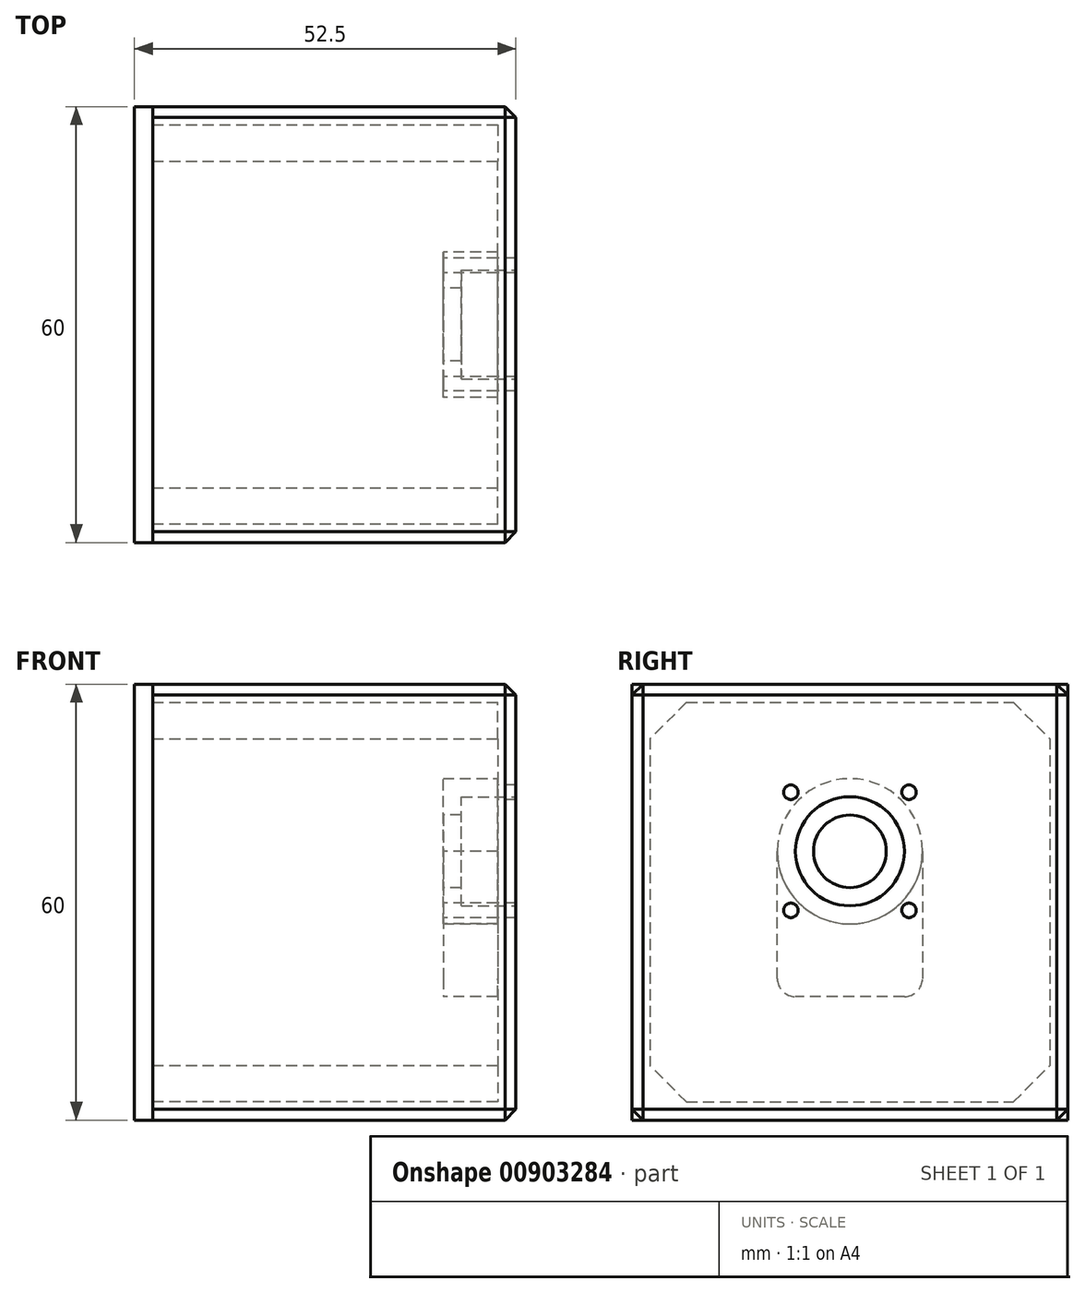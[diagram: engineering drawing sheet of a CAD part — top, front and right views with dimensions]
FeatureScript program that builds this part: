
annotation { "Feature Type Name" : "Feature", "Feature Type Description" : "" }
export const myFeature = defineFeature(function(context is Context, id is Id, definition is map)
    precondition{}
    {
        {
            var Q0;
            Q0=qCreatedBy(makeId("Right.planeOp"),FACE);
            var sketch = newSketch(context, id + "F0", { "sketchPlane" : qUnion([Q0])});
            skLineSegment(sketch, "E0.bottom", {"start": v(-30, 63) * mm, "end": v(30, 63) * mm});
            skLineSegment(sketch, "E0.top", {"start": v(-30, 3) * mm, "end": v(0, 3) * mm});
            skLineSegment(sketch, "E0.left", {"start": v(-30, 63) * mm, "end": v(-30, 3) * mm});
            skLineSegment(sketch, "E0.right", {"start": v(30, 63) * mm, "end": v(30, 3) * mm});
            skLineSegment(sketch, "E1", {"start": v(0, 0) * mm, "end": v(0, 0) * mm});
            skLineSegment(sketch, "E2", {"start": v(0, 0) * mm, "end": v(0, 3) * mm, "construction": true});
            skLineSegment(sketch, "E3", {"start": v(0, 3) * mm, "end": v(30, 3) * mm});
            skSolve(sketch);
        }
        {
            var Q0;
            Q0=makeQuery(id+"F0.imprint","IMPRINT",FACE,{"disambiguationData":[TD([[makeQuery(id+"F0.imprint","IMPRINT",EDGE,{"derivedFrom":sQuery(id+"F0.wireOp",EDGE,"E0.bottom")}),-1.0]])]});
            extrude(context, id + "F1", {"entities" : qUnion([Q0]), "depth" : 50 * mm, "offsetDistance" : 25 * mm});
        }
        {
            var Q0;
            Q0=makeQuery(id+"F1.opExtrude","CAP_FACE",FACE,{"disambiguationData":[OSD([sQuery(id+"F0.wireOp",EDGE,"E0.bottom"),sQuery(id+"F0.wireOp",EDGE,"E0.top"),sQuery(id+"F0.wireOp",EDGE,"E0.left"),sQuery(id+"F0.wireOp",EDGE,"E0.right"),sQuery(id+"F0.wireOp",EDGE,"E3")])],"isStart":false});
            var sketch = newSketch(context, id + "F2", { "sketchPlane" : qUnion([Q0])});
            skCircle(sketch, "E4", {"center": v(0, 40) * mm, "radius": 7.5 * mm});
            skSolve(sketch);
        }
        {
            var Q0;
            Q0=makeQuery(id+"F2.imprint","IMPRINT",FACE,{"disambiguationData":[TD([[makeQuery(id+"F2.imprint","IMPRINT",EDGE,{"derivedFrom":sQuery(id+"F2.wireOp",EDGE,"E4")}),1.0]])]});
            var Q1;
            Q1=sQuery(id+"F2.wireOp",EDGE,"E4");
            extrude(context, id + "F3", {"entities" : qUnion([Q0]), "operationType" : NewBodyOperationType.REMOVE, "surfaceEntities" : qUnion([Q1]), "oppositeDirection" : true, "depth" : 7.5 * mm, "offsetDistance" : 25 * mm});
        }
        {
            var Q0;
            Q0=makeQuery(id+"F1.opExtrude","CAP_FACE",FACE,{"disambiguationData":[OSD([sQuery(id+"F0.wireOp",EDGE,"E0.bottom"),sQuery(id+"F0.wireOp",EDGE,"E0.top"),sQuery(id+"F0.wireOp",EDGE,"E0.left"),sQuery(id+"F0.wireOp",EDGE,"E0.right"),sQuery(id+"F0.wireOp",EDGE,"E3")])],"isStart":true});
            shell(context, id + "F4", {"entities" : qUnion([Q0]), "thickness" : 2.5 * mm});
        }
        {
            var Q0;
            Q0 = qSketchRegion(id + "F0", true);
            extrude(context, id + "F5", {"entities" : qUnion([Q0]), "oppositeDirection" : true, "depth" : 2.5 * mm, "offsetDistance" : 25 * mm});
        }
        {
            var Q0;
            {var subQ0=sQuery(id+"F2.wireOp",EDGE,"E4");Q0=makeQuery(id+"F4.opShell","OFFSET_FACE",FACE,{"disambiguationData":[OSD([subQ0]),TDD([makeQuery(id+"F3.boolean.opBoolean","COPY",FACE,{"derivedFrom":makeQuery(id+"F3.opExtrude","CAP_FACE",FACE,{"disambiguationData":[OSD([subQ0])],"isStart":false})})])]});}
            var sketch = newSketch(context, id + "F6", { "sketchPlane" : qUnion([Q0])});
            skCircle(sketch, "E5", {"center": v(0, 40) * mm, "radius": 5 * mm});
            skSolve(sketch);
        }
        {
            var Q0;
            Q0=makeQuery(id+"F6.imprint","IMPRINT",FACE,{"disambiguationData":[TD([[makeQuery(id+"F6.imprint","IMPRINT",EDGE,{"derivedFrom":sQuery(id+"F6.wireOp",EDGE,"E5")}),1.0]])]});
            extrude(context, id + "F7", {"entities" : qUnion([Q0]), "operationType" : NewBodyOperationType.REMOVE, "oppositeDirection" : true, "depth" : 25 * mm, "offsetDistance" : 25 * mm});
        }
        {
            var Q0;
            {var subQ0=sQuery(id+"F2.wireOp",EDGE,"E4");Q0=makeQuery(id+"F4.opShell","OFFSET_FACE",FACE,{"disambiguationData":[OSD([subQ0]),TDD([makeQuery(id+"F3.boolean.opBoolean","COPY",FACE,{"derivedFrom":makeQuery(id+"F3.opExtrude","CAP_FACE",FACE,{"disambiguationData":[OSD([subQ0])],"isStart":false})})])]});}
            var sketch = newSketch(context, id + "F8", { "sketchPlane" : qUnion([Q0])});
            skLineSegment(sketch, "E6", {"start": v(-10, 40) * mm, "end": v(-10, 20) * mm});
            skLineSegment(sketch, "E7", {"start": v(-10, 20) * mm, "end": v(10, 20) * mm});
            skLineSegment(sketch, "E8", {"start": v(10, 20) * mm, "end": v(10, 40) * mm});
            skSolve(sketch);
        }
        {
            var Q0;
            Q0=makeQuery(id+"F1.opExtrude","SWEPT_EDGE",EDGE,{"disambiguationData":[OSD([sQuery(id+"F0.wireOp",EDGE,"E0.right"),sQuery(id+"F0.wireOp",EDGE,"E3")])]});
            var Q1;
            Q1=makeQuery(id+"F1.opExtrude","SWEPT_EDGE",EDGE,{"disambiguationData":[OSD([sQuery(id+"F0.wireOp",EDGE,"E0.bottom"),sQuery(id+"F0.wireOp",EDGE,"E0.right")])]});
            var Q2;
            Q2=makeQuery(id+"F1.opExtrude","SWEPT_EDGE",EDGE,{"disambiguationData":[OSD([sQuery(id+"F0.wireOp",EDGE,"E0.top"),sQuery(id+"F0.wireOp",EDGE,"E0.left")])]});
            var Q3;
            Q3=makeQuery(id+"F1.opExtrude","SWEPT_EDGE",EDGE,{"disambiguationData":[OSD([sQuery(id+"F0.wireOp",EDGE,"E0.bottom"),sQuery(id+"F0.wireOp",EDGE,"E0.left")])]});
            var Q4;
            Q4=makeQuery(id+"F1.opExtrude","CAP_EDGE",EDGE,{"disambiguationData":[OSD([sQuery(id+"F0.wireOp",EDGE,"E0.bottom")])],"isStart":false});
            var Q5;
            Q5=makeQuery(id+"F1.opExtrude","CAP_EDGE",EDGE,{"disambiguationData":[OSD([sQuery(id+"F0.wireOp",EDGE,"E0.left")])],"isStart":false});
            var Q6;
            Q6=makeQuery(id+"F1.opExtrude","CAP_EDGE",EDGE,{"disambiguationData":[OSD([sQuery(id+"F0.wireOp",EDGE,"E0.right")])],"isStart":false});
            var Q7;
            Q7=makeQuery(id+"F1.opExtrude","CAP_EDGE",EDGE,{"disambiguationData":[OSD([sQuery(id+"F0.wireOp",EDGE,"E0.top"),sQuery(id+"F0.wireOp",EDGE,"E3")])],"isStart":false});
            chamfer(context, id + "F9", {"entities" : qUnion([Q0, Q1, Q2, Q3, Q4, Q5, Q6, Q7]), "width" : 1.5 * mm, "tangentPropagation" : true});
        }
        {
            var Q0;
            {var subQ0=sQuery(id+"F8.wireOp",EDGE,"E6");Q0=makeQuery(id+"F8.imprint","IMPRINT",FACE,{"disambiguationData":[TD([[makeQuery(id+"F8.imprint","IMPRINT",EDGE,{"derivedFrom":subQ0}),1.0]])]});}
            extrude(context, id + "F10", {"entities" : qUnion([Q0]), "endBound" : BoundingType.UP_TO_NEXT, "oppositeDirection" : true, "depth" : 25 * mm, "offsetDistance" : 25 * mm});
        }
        {
            var Q0;
            Q0=makeQuery(id+"F4.opShell","OFFSET_EDGE",EDGE,{"disambiguationData":[OSD([sQuery(id+"F0.wireOp",EDGE,"E0.right"),sQuery(id+"F0.wireOp",EDGE,"E3")])]});
            var Q1;
            Q1=makeQuery(id+"F4.opShell","OFFSET_EDGE",EDGE,{"disambiguationData":[OSD([sQuery(id+"F0.wireOp",EDGE,"E0.top"),sQuery(id+"F0.wireOp",EDGE,"E0.left")])]});
            var Q2;
            Q2=makeQuery(id+"F4.opShell","OFFSET_EDGE",EDGE,{"disambiguationData":[OSD([sQuery(id+"F0.wireOp",EDGE,"E0.bottom"),sQuery(id+"F0.wireOp",EDGE,"E0.left")])]});
            var Q3;
            Q3=makeQuery(id+"F4.opShell","OFFSET_EDGE",EDGE,{"disambiguationData":[OSD([sQuery(id+"F0.wireOp",EDGE,"E0.bottom"),sQuery(id+"F0.wireOp",EDGE,"E0.right")])]});
            chamfer(context, id + "F11", {"entities" : qUnion([Q0, Q1, Q2, Q3]), "width" : 5 * mm, "tangentPropagation" : true});
        }
        {
            var Q0;
            Q0=makeQuery(id+"F10.opExtrude","SWEPT_EDGE",EDGE,{"disambiguationData":[OSD([sQuery(id+"F8.wireOp",EDGE,"E7"),sQuery(id+"F8.wireOp",EDGE,"E8")])]});
            var Q1;
            Q1=makeQuery(id+"F10.opExtrude","SWEPT_EDGE",EDGE,{"disambiguationData":[OSD([sQuery(id+"F8.wireOp",EDGE,"E6"),sQuery(id+"F8.wireOp",EDGE,"E7")])]});
            fillet(context, id + "F12", {"entities" : qUnion([Q0, Q1]), "radius" : 2.5 * mm, "tangentPropagation" : true, "allowEdgeOverflow" : false});
        }
        {
            var Q0;
            Q0=makeQuery(id+"F1.opExtrude","CAP_FACE",FACE,{"disambiguationData":[OSD([sQuery(id+"F0.wireOp",EDGE,"E0.bottom"),sQuery(id+"F0.wireOp",EDGE,"E0.top"),sQuery(id+"F0.wireOp",EDGE,"E0.left"),sQuery(id+"F0.wireOp",EDGE,"E0.right"),sQuery(id+"F0.wireOp",EDGE,"E3")])],"isStart":false});
            var sketch = newSketch(context, id + "F13", { "sketchPlane" : qUnion([Q0])});
            skCircle(sketch, "E9", {"center": v(0, 40) * mm, "radius": 11.5 * mm, "construction": true});
            skLineSegment(sketch, "E10.bottom", {"start": v(8.13, 31.87) * mm, "end": v(-8.13, 31.87) * mm, "construction": true});
            skLineSegment(sketch, "E10.top", {"start": v(8.13, 48.13) * mm, "end": v(-8.13, 48.13) * mm, "construction": true});
            skLineSegment(sketch, "E10.left", {"start": v(8.13, 31.87) * mm, "end": v(8.13, 48.13) * mm, "construction": true});
            skLineSegment(sketch, "E10.right", {"start": v(-8.13, 31.87) * mm, "end": v(-8.13, 48.13) * mm, "construction": true});
            skCircle(sketch, "E11", {"center": v(-8.13, 48.13) * mm, "radius": 1 * mm});
            skCircle(sketch, "E12", {"center": v(8.13, 48.13) * mm, "radius": 1 * mm});
            skCircle(sketch, "E13", {"center": v(-8.13, 31.87) * mm, "radius": 1 * mm});
            skCircle(sketch, "E14", {"center": v(8.13, 31.87) * mm, "radius": 1 * mm});
            skSolve(sketch);
        }
        {
            var Q0;
            Q0=sQuery(id+"F13.wireOp",VERTEX,"E10.left.end");
            var Q1;
            Q1=sQuery(id+"F13.wireOp",VERTEX,"E10.bottom.start");
            var Q2;
            Q2=sQuery(id+"F13.wireOp",VERTEX,"E13.center");
            var Q3;
            Q3=sQuery(id+"F13.wireOp",VERTEX,"E11.center");
            var Q4;
            Q4=makeQuery(id+"F1.opExtrude","SWEPT_BODY",BODY,{"disambiguationData":[OSD([sQuery(id+"F0.wireOp",EDGE,"E0.bottom"),sQuery(id+"F0.wireOp",EDGE,"E0.top"),sQuery(id+"F0.wireOp",EDGE,"E0.left"),sQuery(id+"F0.wireOp",EDGE,"E0.right"),sQuery(id+"F0.wireOp",EDGE,"E3")])]});
            var Q5;
            Q5=makeQuery(id+"F10.opExtrude","SWEPT_BODY",BODY,{"disambiguationData":[OSD([sQuery(id+"F2.wireOp",EDGE,"E4"),sQuery(id+"F8.wireOp",EDGE,"E6"),sQuery(id+"F8.wireOp",EDGE,"E7"),sQuery(id+"F8.wireOp",EDGE,"E8")])]});
            hole(context, id + "F14", {"style" : HoleStyle.SIMPLE, "endStyle" : HoleEndStyle.THROUGH, "holeDiameter" : 2 * mm, "majorDiameter" : 5 * mm, "isTappedThrough" : true, "tappedDepth" : 12 * mm, "tapClearance" : 3, "locations" : qUnion([Q0, Q1, Q2, Q3]), "scope" : qUnion([Q4, Q5])});
        }
    });
